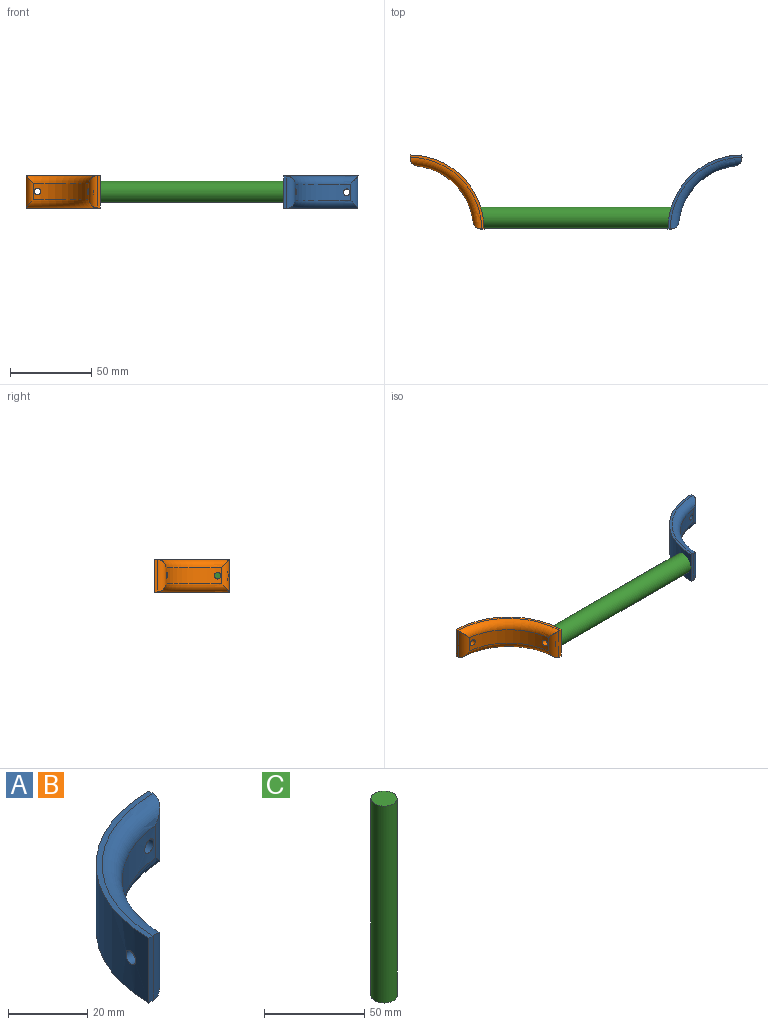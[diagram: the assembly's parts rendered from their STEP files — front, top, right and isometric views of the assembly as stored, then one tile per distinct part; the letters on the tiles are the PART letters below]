
ASSEMBLY  parts=3 mates=1
PART A: 12 faces, bbox 51.5x51.5x20 mm
  f0: cylinder r=39mm len=34.32mm, axis (0,0,-1), area 498.2mm2, adj f6,f7,f8,f9,f10,f11
  f1: plane 20x1.8mm, normal (1,0,0), area 35.9mm2, adj f2,f4,f5,f7,f8,f9
  f2: cylinder r=45.51mm len=45.51mm, axis (0,0,-1), area 1404.3mm2, adj f1,f3,f4,f5,f10,f11
  f3: plane 20x1.8mm, normal (0,-1,0), area 35.9mm2, adj f2,f4,f5,f6,f7,f8
  f4: plane 45.51x45.51mm, normal (0,0,1), area 106.3mm2, adj f1,f2,f3,f7
  f5: plane 45.51x45.51mm, normal (0,0,-1), area 106.3mm2, adj f1,f2,f3,f8
  f6: cylinder r=5mm len=19.98mm, axis (0,0,-1), area 118.6mm2, adj f0,f3,f7,f8
  f7: torus R=44mm, axis (0,0,1), area 479.1mm2, adj f0,f1,f3,f4,f6,f9
  f8: torus R=44mm, axis (0,0,1), area 479.1mm2, adj f0,f1,f3,f5,f6,f9
  f9: cylinder r=5mm len=19.98mm, axis (0,0,-1), area 118.6mm2, adj f0,f1,f7,f8
  f10: cylinder r=2mm len=7.29mm, axis (1,0,0), area 83mm2, adj f0,f2
  f11: cylinder r=2mm len=7.29mm, axis (0,-1,0), area 83mm2, adj f0,f2
PART B: same geometry as A
PART C: 3 faces, bbox 13x13x120 mm
  f0: cylinder r=6.5mm len=120mm, axis (0,0,-1), area 4900.9mm2, adj f1,f2
  f1: plane 13x13mm, normal (0,0,1), area 132.7mm2, adj f0
  f2: plane 13x13mm, normal (0,0,-1), area 132.7mm2, adj f0
PLACE A rot(axis=(0.32,0.08,0.95),0deg) t=(33.08,6.1,6.46)mm
PLACE B rot(axis=(0,0,-1),90deg) t=(-171.1,6.1,6.74)mm
PLACE C rot(axis=(0,1,0),90deg) t=(-129.51,13.1,16.74)mm
MATE revolute C.f0 <-> B.f11  axis (-1,0,0) through (-129.51,13.1,16.74)mm
